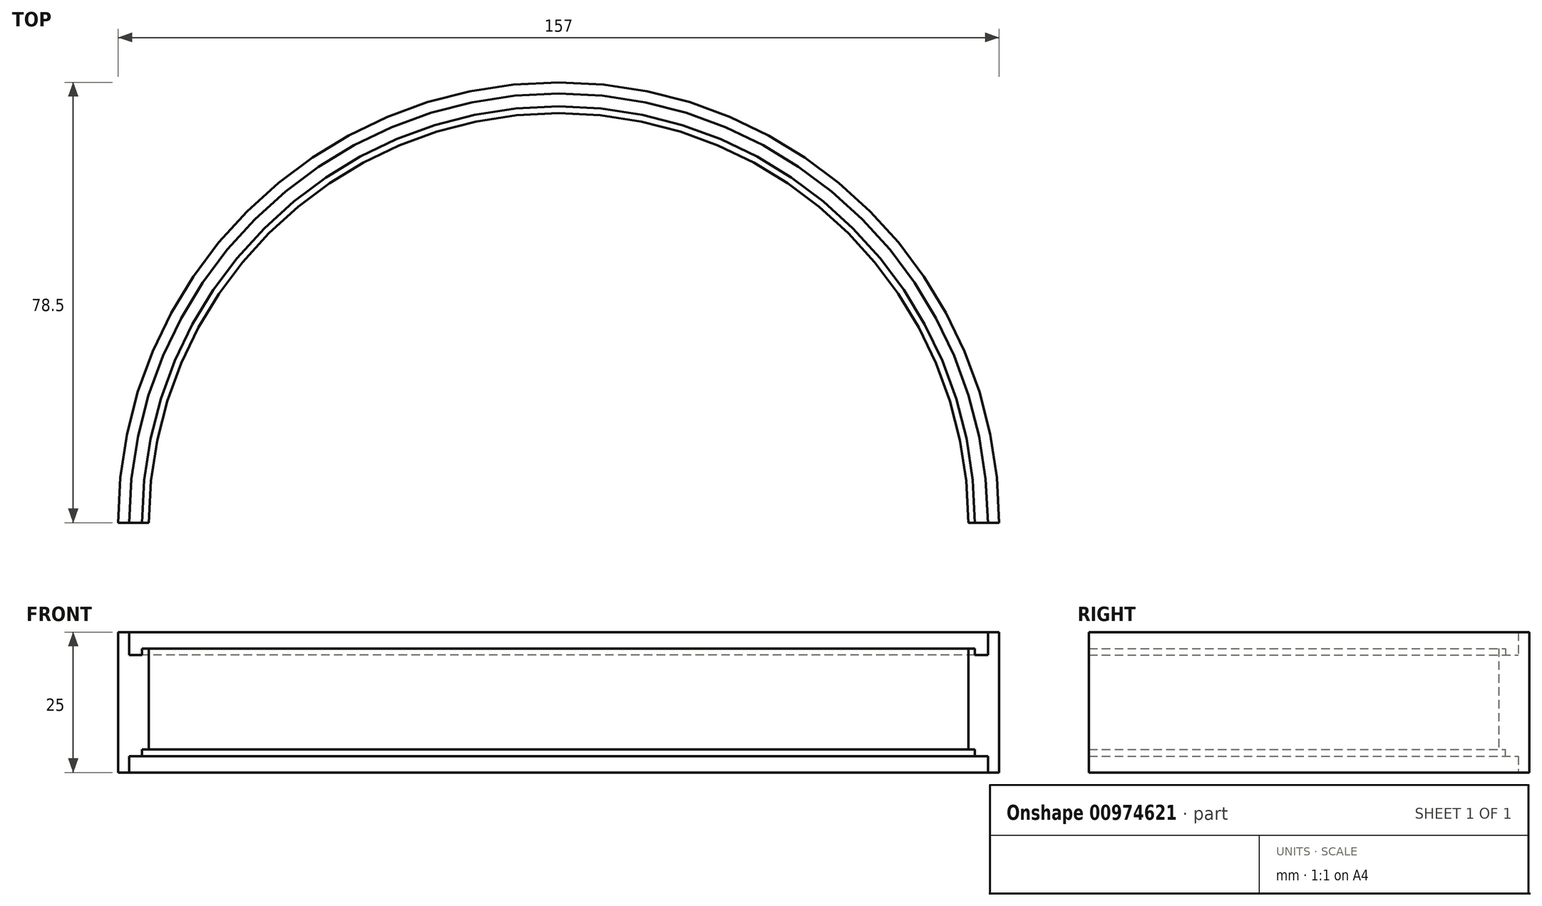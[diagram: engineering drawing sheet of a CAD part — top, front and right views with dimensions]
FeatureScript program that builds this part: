
annotation { "Feature Type Name" : "Feature", "Feature Type Description" : "" }
export const myFeature = defineFeature(function(context is Context, id is Id, definition is map)
    precondition{}
    {
        {
            var Q0;
            Q0=qCreatedBy(makeId("Top.planeOp"),FACE);
            var sketch = newSketch(context, id + "F0", { "sketchPlane" : qUnion([Q0])});
            skArc(sketch, "E0", {"start": v(76.5, 0) * mm, "mid": v(0, 76.5) * mm, "end": v(-76.5, 0) * mm});
            skArc(sketch, "E1.0", {"start": v(78.5, 0) * mm, "mid": v(0, 78.5) * mm, "end": v(-78.5, 0) * mm});
            skLineSegment(sketch, "E2", {"start": v(-78.5, 0) * mm, "end": v(-76.5, 0) * mm});
            skLineSegment(sketch, "E3", {"start": v(76.5, 0) * mm, "end": v(78.5, 0) * mm});
            skSolve(sketch);
        }
        {
            var Q0;
            Q0=makeQuery(id+"F0.imprint","IMPRINT",FACE,{"disambiguationData":[TD([[makeQuery(id+"F0.imprint","IMPRINT",EDGE,{"derivedFrom":sQuery(id+"F0.wireOp",EDGE,"E0")}),-1.0]])]});
            extrude(context, id + "F1", {"entities" : qUnion([Q0]), "depth" : 25 * mm});
        }
        {
            var Q0;
            Q0=qCreatedBy(makeId("Top.planeOp"),FACE);
            cPlane(context, id + "F2", {"entities" : qUnion([Q0]), "cplaneType" : CPlaneType.OFFSET, "offset" : 4.1 * mm, "width" : 150 * mm, "height" : 150 * mm});
        }
        {
            var Q0;
            Q0=qCreatedBy(id+"F2.planeOp",FACE);
            var sketch = newSketch(context, id + "F3", { "sketchPlane" : qUnion([Q0])});
            skArc(sketch, "E4", {"start": v(76.5, 0) * mm, "mid": v(0, 76.5) * mm, "end": v(-76.5, 0) * mm});
            skArc(sketch, "E5.0", {"start": v(73, 0) * mm, "mid": v(0, 73) * mm, "end": v(-73, 0) * mm});
            skLineSegment(sketch, "E6", {"start": v(-76.5, 0) * mm, "end": v(-73, 0) * mm});
            skLineSegment(sketch, "E7", {"start": v(73, 0) * mm, "end": v(76.5, 0) * mm});
            skSolve(sketch);
        }
        {
            var Q0;
            Q0=makeQuery(id+"F3.imprint","IMPRINT",FACE,{"disambiguationData":[TD([[makeQuery(id+"F3.imprint","IMPRINT",EDGE,{"derivedFrom":sQuery(id+"F3.wireOp",EDGE,"E4")}),1.0]])]});
            extrude(context, id + "F4", {"entities" : qUnion([Q0]), "operationType" : NewBodyOperationType.ADD, "depth" : 16.8 * mm});
        }
        {
            var Q0;
            Q0=makeQuery(id+"F4.opExtrude","CAP_FACE",FACE,{"disambiguationData":[OSD([sQuery(id+"F3.wireOp",EDGE,"E4"),sQuery(id+"F3.wireOp",EDGE,"E5.0"),sQuery(id+"F3.wireOp",EDGE,"E6"),sQuery(id+"F3.wireOp",EDGE,"E7")])],"isStart":false});
            var sketch = newSketch(context, id + "F5", { "sketchPlane" : qUnion([Q0])});
            skArc(sketch, "E8.0", {"start": v(74.2, 0) * mm, "mid": v(0, 74.2) * mm, "end": v(-74.2, 0) * mm});
            skSolve(sketch);
        }
        {
            var Q0;
            {var subQ0=sQuery(id+"F5.wireOp",EDGE,"E8.0");Q0=makeQuery(id+"F5.imprint","IMPRINT",FACE,{"disambiguationData":[TD([[makeQuery(id+"F5.imprint","IMPRINT",EDGE,{"derivedFrom":subQ0}),1.0]])]});}
            extrude(context, id + "F6", {"entities" : qUnion([Q0]), "operationType" : NewBodyOperationType.ADD, "depth" : 1.2 * mm});
        }
        {
            var Q0;
            Q0=makeQuery(id+"F4.opExtrude","CAP_FACE",FACE,{"disambiguationData":[OSD([sQuery(id+"F3.wireOp",EDGE,"E4"),sQuery(id+"F3.wireOp",EDGE,"E5.0"),sQuery(id+"F3.wireOp",EDGE,"E6"),sQuery(id+"F3.wireOp",EDGE,"E7")])],"isStart":true});
            var sketch = newSketch(context, id + "F7", { "sketchPlane" : qUnion([Q0])});
            skArc(sketch, "E9.0", {"start": v(74.2, 0) * mm, "mid": v(0, -74.2) * mm, "end": v(-74.2, 0) * mm});
            skSolve(sketch);
        }
        {
            var Q0;
            {var subQ0=sQuery(id+"F7.wireOp",EDGE,"E9.0");Q0=makeQuery(id+"F7.imprint","IMPRINT",FACE,{"disambiguationData":[TD([[makeQuery(id+"F7.imprint","IMPRINT",EDGE,{"derivedFrom":subQ0}),-1.0]])]});}
            extrude(context, id + "F8", {"entities" : qUnion([Q0]), "operationType" : NewBodyOperationType.ADD, "depth" : 1.2 * mm});
        }
    });
